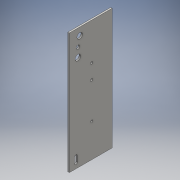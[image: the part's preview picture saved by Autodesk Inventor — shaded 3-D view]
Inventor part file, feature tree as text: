
AUTODESK INVENTOR PART (.ipt)
format: ipt  version: 2016 (Build 200138000, 138)  size: 125,952 bytes
history: native  units: mm
features: extrude x1, sketch x1
ambient origin geometry x8: Origin, YZ Plane, XZ Plane, XY Plane, X Axis, Y Axis, Z Axis, Center Point
bodies: Body1 (feature_tree)
feature tree (2):
  extrude  "Extrusion2"  Depth=128.0mm
  sketch  "Sketch1"  dims[d0=45.3mm d1=128.0mm d2=6.0mm d3=4.0mm d4=6.0mm d5=8.0mm d6=17.5mm d7=27.0mm d8=11.0mm d9=9.0mm d10=9.0mm d11=2.5mm d12=39.25mm d13=23.5mm d14=2.5mm d15=54.75mm d16=23.5mm d17=2.5mm d18=23.5mm d19=92.75mm d20=3.0mm d21=9.0mm d22=115.0mm d23=5.5mm d27=6.0mm d28=1.5mm d29=6.0mm d30=1.6mm d31=0.0mm]
